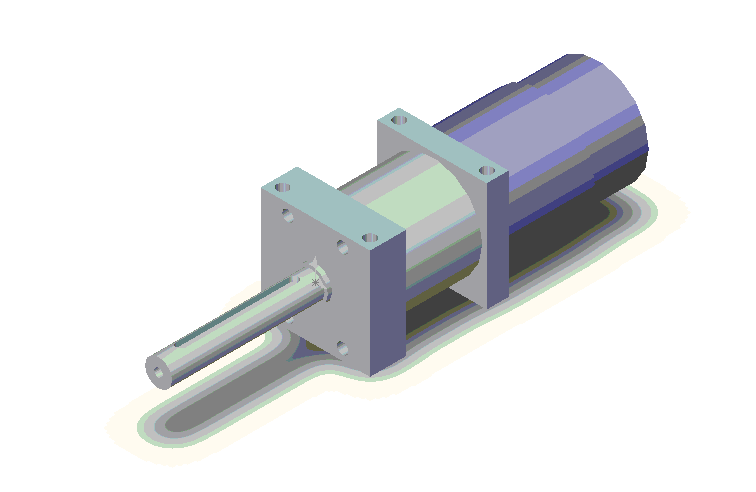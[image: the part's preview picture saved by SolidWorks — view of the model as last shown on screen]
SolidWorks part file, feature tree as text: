
SOLIDWORKS PART (.sldprt)
format: sldprt  version: not decoded by parser v0  size: 543,744 bytes
history: native  units: mm
features: sketch x14, extrude x7, cut_extrude x7, plane x2 (+8 scaffold rows collapsed)
feature tree (38):
  scaffold x8  (default folders/planes/origin — collapsed)
  sketch  "Sketch1"  dims[D13=4.0mm D14=4.0mm D15=4.0mm D16=4.0mm D1=19.05mm D2=38.1mm D3=19.05mm D4=38.1mm D5=9.525mm D6=9.53mm D7=9.53mm D8=9.53mm D9=3.81mm D10=3.81mm D11=34.29mm D12=34.29mm]
  extrude  "Base-Extrude"  Depth=12.7mm
  sketch  "Sketch2"  dims[D1=9.525mm]
  extrude  "Boss-Extrude1"  Depth=54.61mm
  plane  "Plane1"
  sketch  "Sketch3"  dims[D1=3.175mm D2=3.175mm D3=7.62mm D4=39.37mm]
  plane  "Plane2"  Offset=2.7625mm
  cut_extrude  "Cut-Extrude3"  [1 undecoded]
  sketch  "Sketch4"  dims[D1=3.0mm]
  cut_extrude  "Cut-Extrude4"  Depth=9.525mm
  sketch  "Sketch5"
  extrude  "Boss-Extrude2"  Depth=1.5mm
  sketch  "Sketch6"  dims[D1=4.0mm D2=4.0mm D3=3.81mm D4=34.29mm D5=3.81mm D6=3.81mm]
  cut_extrude  "Cut-Extrude5"  Depth=9.5mm
  sketch  "Sketch7"  dims[D1=15.24mm]
  cut_extrude  "Cut-Extrude6"  Depth=9.5mm
  sketch  "Sketch8"  dims[D1=35.0mm]
  extrude  "Boss-Extrude3"  Depth=27.94mm
  sketch  "Sketch9"
  extrude  "Boss-Extrude4"  Depth=7.62mm
  sketch  "Sketch11"  dims[D7=4.0mm D8=4.0mm D9=4.0mm D10=4.0mm D11=4.0mm D12=4.0mm D13=4.0mm D14=4.0mm D1=9.525mm D2=9.525mm D3=28.575mm D4=28.575mm D5=3.81mm D6=34.29mm D15=3.81mm D16=9.53mm D17=28.58mm D18=34.29mm]
  cut_extrude  "Cut-Extrude7"  Depth=9.525mm
  sketch  "Sketch12"  dims[c1.D3=4.0mm c1.D4=4.0mm c1.D1=3.81mm c1.D2=3.81mm c2.D3=3.81mm c2.D5=3.81mm]
  cut_extrude  "Cut-Extrude8"  Depth=9.525mm
  sketch  "Sketch13"
  cut_extrude  "Cut-Extrude9"  Depth=9.525mm
  sketch  "Sketch14"  dims[D1=35.814mm]
  extrude  "Boss-Extrude5"  Depth=50mm
  sketch  "Sketch15"  dims[D1=38.1mm]
  extrude  "Boss-Extrude6"  Depth=30mm
decode coverage: 24 of 28 modeling features carry decoded parameters
note: 1 parameter value undecoded
note: suppression state not decoded; provenance and decode notes live in map.json
